# Revit family: 820-10-029-DN25-65
name_source: partatom
category: Pipe Accessories
units: mm (PartAtom-declared; Revit-internal decimal feet)

## family parameters
Always vertical = Yes
Cut with Voids When Loaded = No
Part Type = Valve - Breaks Into
Round Connector Dimension = Use Diameter
Shared = No
Work Plane-Based = No

## types (5) — shared parameters
2 = 2 mm  [stored 0.00656168 ft]
90 = 90 mm
Actuator_Dia = 65 mm  [stored 0.213255 ft]
Body_wallthickness = 10 mm  [stored 0.0328084 ft]
DN25_PN10/16 = 820-0025-10-541L0160002
DN32_PN10/16 = 820-0032-10-541L0160002
DN40_PN10/16 = 820-0040-10-541L0160002
DN50_PN10/16 = 820-0050-10-541L0160002
DN65_PN10/16 = 820-0065-10-541L0160002
Description_ = AVK CENTRIC BUTTERFLY VALVE LUG TYPE, PN10/16
F2 = 12 mm  [stored 0.0393701 ft]
Search_table = 820-10-029-DN25-65
URL product pages = https://www.avkvalves.com
fillet = 20 mm  [stored 0.0656168 ft]
zero-valued in all types: Default Elevation

## per-type parameters (varying)
| type | Actuator FL_D | Bore | DN | EPDM | F | Flange_thickness | H2 | Hole_dia | ID | L | L2 | LUG_T | L_ref | L_ref_2 | L_ref_3 | Lug_D | PCD | Rubber_R | W2_ref | disk |
| DN25_PN10/16 | 50 mm  [stored 0.164042 ft] | 13 mm  [stored 0.0426509 ft] | 25 mm  [stored 0.082021 ft] | 12 mm  [stored 0.0393701 ft] | 8 mm  [stored 0.0262467 ft] | 6 mm  [stored 0.019685 ft] | 51 mm  [stored 0.167323 ft] | 14 mm  [stored 0.0459318 ft] | 13 mm  [stored 0.0426509 ft] | 30 mm  [stored 0.0984252 ft] | 51 mm  [stored 0.167323 ft] | 12 mm  [stored 0.0393701 ft] | 18 mm  [stored 0.0590551 ft] | 36 mm  [stored 0.11811 ft] | 15 mm  [stored 0.0492126 ft] | 10 mm  [stored 0.0328084 ft] | 43 mm  [stored 0.141076 ft] | 18 mm  [stored 0.0590551 ft] | 110 mm | 8 mm  [stored 0.0262467 ft] |
| DN32_PN10/16 | 60 mm  [stored 0.19685 ft] | 16 mm  [stored 0.0524934 ft] | 32 mm  [stored 0.104987 ft] | 15 mm  [stored 0.0492126 ft] | 8 mm  [stored 0.0262467 ft] | 6 mm  [stored 0.019685 ft] | 51 mm  [stored 0.167323 ft] | 19 mm  [stored 0.062336 ft] | 16 mm  [stored 0.0524934 ft] | 30 mm  [stored 0.0984252 ft] | 51 mm  [stored 0.167323 ft] | 12 mm  [stored 0.0393701 ft] | 18 mm  [stored 0.0590551 ft] | 36 mm  [stored 0.11811 ft] | 15 mm  [stored 0.0492126 ft] | 13 mm  [stored 0.0426509 ft] | 50 mm  [stored 0.164042 ft] | 21 mm  [stored 0.0688976 ft] | 110 mm | 8 mm  [stored 0.0262467 ft] |
| DN40_PN10/16 | 70 mm  [stored 0.229659 ft] | 20 mm  [stored 0.0656168 ft] | 40 mm  [stored 0.131234 ft] | 19 mm  [stored 0.062336 ft] | 8 mm  [stored 0.0262467 ft] | 7 mm  [stored 0.0229659 ft] | 54 mm  [stored 0.177165 ft] | 19 mm  [stored 0.062336 ft] | 20 mm  [stored 0.0656168 ft] | 33 mm  [stored 0.108268 ft] | 54 mm  [stored 0.177165 ft] | 13 mm  [stored 0.0426509 ft] | 19 mm  [stored 0.062336 ft] | 38 mm  [stored 0.124672 ft] | 16 mm  [stored 0.0524934 ft] | 13 mm  [stored 0.0426509 ft] | 55 mm  [stored 0.180446 ft] | 25 mm  [stored 0.082021 ft] | 130 mm | 9 mm  [stored 0.0295276 ft] |
| DN50_PN10/16 | 70 mm  [stored 0.229659 ft] | 25 mm  [stored 0.082021 ft] | 50 mm  [stored 0.164042 ft] | 24 mm  [stored 0.0787402 ft] | 11 mm  [stored 0.0360892 ft] | 7 mm  [stored 0.0229659 ft] | 72 mm  [stored 0.23622 ft] | 19 mm  [stored 0.062336 ft] | 25 mm  [stored 0.082021 ft] | 43 mm  [stored 0.141076 ft] | 58 mm  [stored 0.190289 ft] | 17 mm | 29 mm  [stored 0.0951444 ft] | 58 mm  [stored 0.190289 ft] | 24 mm  [stored 0.0787402 ft] | 13 mm  [stored 0.0426509 ft] | 63 mm  [stored 0.206693 ft] | 30 mm  [stored 0.0984252 ft] | 135 mm | 12 mm  [stored 0.0393701 ft] |
| DN65_PN10/16 | 80 mm | 33 mm  [stored 0.108268 ft] | 65 mm  [stored 0.213255 ft] | 32 mm  [stored 0.104987 ft] | 11 mm  [stored 0.0360892 ft] | 8 mm  [stored 0.0262467 ft] | 82 mm | 19 mm  [stored 0.062336 ft] | 33 mm  [stored 0.108268 ft] | 46 mm  [stored 0.150919 ft] | 66 mm | 18 mm  [stored 0.0590551 ft] | 30 mm  [stored 0.0984252 ft] | 60 mm  [stored 0.19685 ft] | 25 mm  [stored 0.082021 ft] | 13 mm  [stored 0.0426509 ft] | 73 mm | 38 mm  [stored 0.124672 ft] | 150 mm | 13 mm  [stored 0.0426509 ft] |

note: [stored X ft] marks values corroborated as IEEE doubles in the binary element streams (Revit-internal decimal feet)

## geometry (parser evidence)
native form markers: Sweep x4
no freeform markers — native parametric forms only
